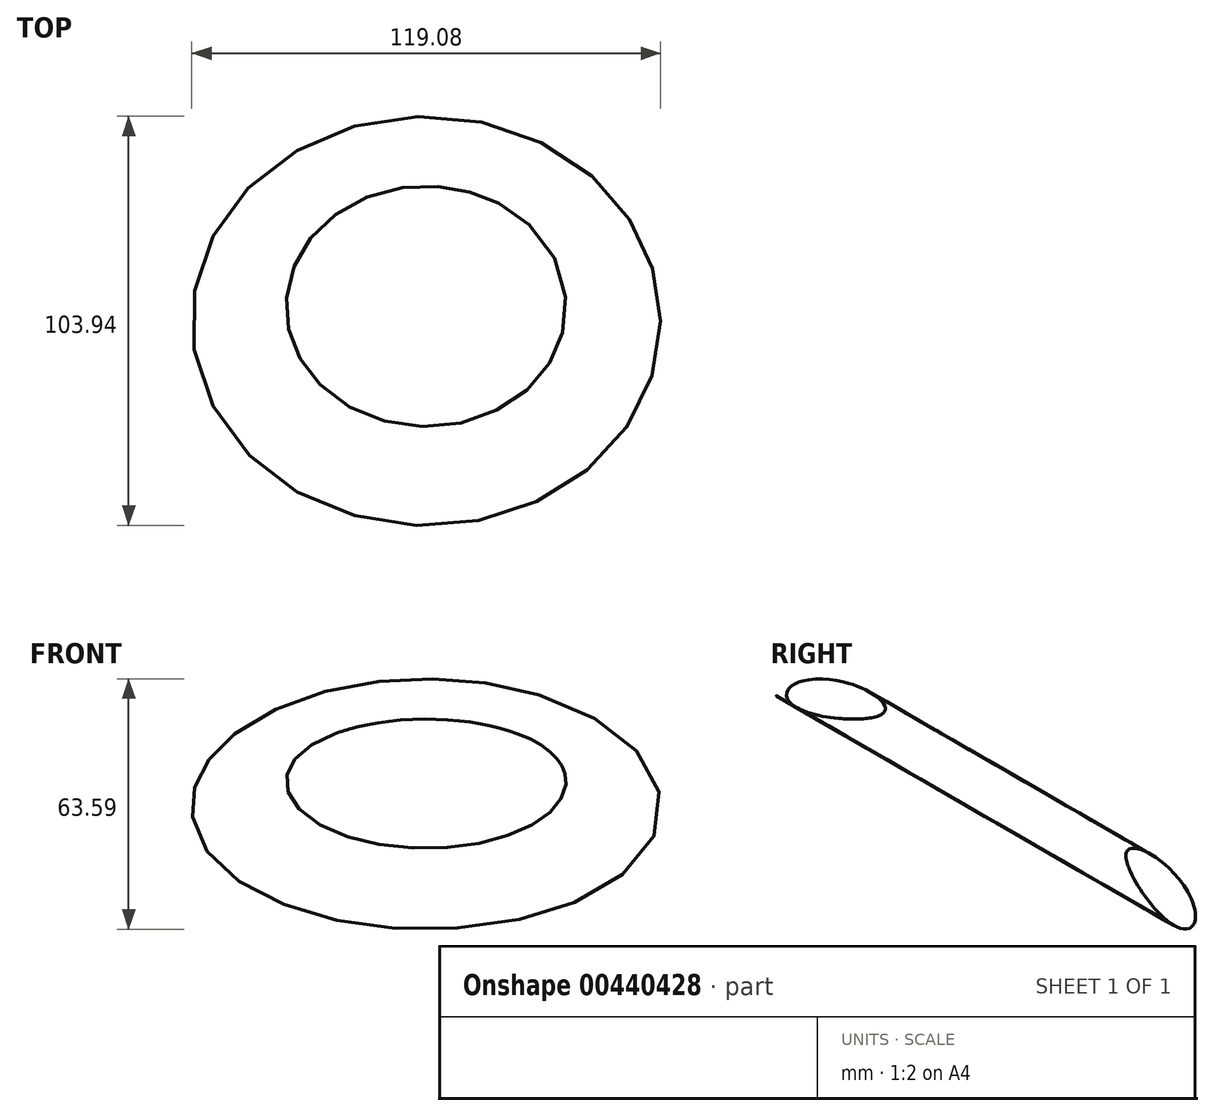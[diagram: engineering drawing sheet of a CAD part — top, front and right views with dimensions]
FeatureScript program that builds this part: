
annotation { "Feature Type Name" : "Feature", "Feature Type Description" : "" }
export const myFeature = defineFeature(function(context is Context, id is Id, definition is map)
    precondition{}
    {
        {
            var Q0;
            Q0=qCreatedBy(makeId("Top.planeOp"),FACE);
            var sketch = newSketch(context, id + "F0", { "sketchPlane" : qUnion([Q0])});
            skCircle(sketch, "E0", {"center": v(-35.92, -35.92) * mm, "radius": 12.7 * mm});
            skLineSegment(sketch, "E1", {"start": v(-35.92, -35.92) * mm, "end": v(0, 0) * mm, "construction": true});
            skLineSegment(sketch, "E2", {"start": v(0, 0) * mm, "end": v(0, -47.3) * mm, "construction": true});
            skSolve(sketch);
        }
        {
            var Q0;
            Q0=qCreatedBy(makeId("Right.planeOp"),FACE);
            var sketch = newSketch(context, id + "F1", { "sketchPlane" : qUnion([Q0])});
            skLineSegment(sketch, "E3", {"start": v(0, 0) * mm, "end": v(25.8, 44.7) * mm});
            skLineSegment(sketch, "E4", {"start": v(0, 0) * mm, "end": v(44.22, 0) * mm});
            skSolve(sketch);
        }
        {
            var Q0;
            Q0=makeQuery(id+"F0.imprint","IMPRINT",FACE,{"disambiguationData":[TD([[makeQuery(id+"F0.imprint","IMPRINT",EDGE,{"derivedFrom":sQuery(id+"F0.wireOp",EDGE,"E0")}),1.0]])]});
            var Q1;
            Q1=sQuery(id+"F1.wireOp",EDGE,"E3");
            revolve(context, id + "F2", {"entities" : qUnion([Q0]), "axis" : qUnion([Q1]), "revolveType" : RevolveType.FULL});
        }
    });
